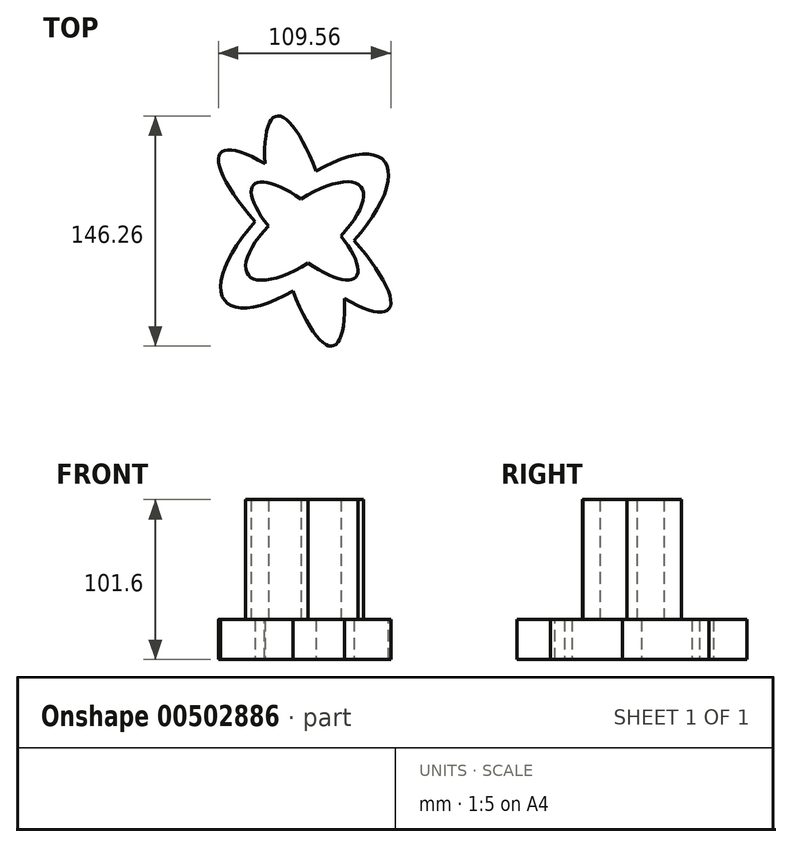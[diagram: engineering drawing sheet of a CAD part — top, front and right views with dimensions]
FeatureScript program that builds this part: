
annotation { "Feature Type Name" : "Feature", "Feature Type Description" : "" }
export const myFeature = defineFeature(function(context is Context, id is Id, definition is map)
    precondition{}
    {
        {
            var Q0;
            Q0=qCreatedBy(makeId("Top.planeOp"),FACE);
            var sketch = newSketch(context, id + "F0", { "sketchPlane" : qUnion([Q0])});
            skEllipse(sketch, "E0", {"center": v(0, 0) * mm, "majorRadius": 67.32 * mm, "minorRadius": 26.5 * mm, "majorAxis": v(0.75, 0.66)});
            skEllipse(sketch, "E1", {"center": v(0, 0) * mm, "majorRadius": 72.96 * mm, "minorRadius": 18.45 * mm, "majorAxis": v(-0.73, 0.68)});
            skSolve(sketch);
        }
        {
            var Q0;
            {var subQ0=sQuery(id+"F0.wireOp",EDGE,"E1");var subQ1=sQuery(id+"F0.wireOp",EDGE,"E0");var subQ2=makeQuery(id+"F0.imprint","INTERSECT",VERTEX,{"disambiguationData":[OD(1.0)],"derivedFrom":[subQ1,subQ0]});Q0=makeQuery(id+"F0.imprint","IMPRINT",FACE,{"disambiguationData":[TD([[makeQuery(id+"F0.imprint","IMPRINT",EDGE,{"disambiguationData":[TD([[subQ2,1.0]])],"derivedFrom":subQ1}),1.0]])]});}
            var Q1;
            {var subQ0=sQuery(id+"F0.wireOp",EDGE,"E1");var subQ1=sQuery(id+"F0.wireOp",EDGE,"E0");var subQ2=makeQuery(id+"F0.imprint","INTERSECT",VERTEX,{"disambiguationData":[OD(0.0)],"derivedFrom":[subQ1,subQ0]});Q1=makeQuery(id+"F0.imprint","IMPRINT",FACE,{"disambiguationData":[TD([[makeQuery(id+"F0.imprint","IMPRINT",EDGE,{"disambiguationData":[TD([[subQ2,1.0]])],"derivedFrom":subQ1}),1.0]])]});}
            var Q2;
            {var subQ0=sQuery(id+"F0.wireOp",EDGE,"E1");var subQ1=sQuery(id+"F0.wireOp",EDGE,"E0");var subQ2=makeQuery(id+"F0.imprint","INTERSECT",VERTEX,{"disambiguationData":[OD(0.0)],"derivedFrom":[subQ1,subQ0]});Q2=makeQuery(id+"F0.imprint","IMPRINT",FACE,{"disambiguationData":[TD([[makeQuery(id+"F0.imprint","IMPRINT",EDGE,{"disambiguationData":[TD([[subQ2,-1.0]])],"derivedFrom":subQ1}),1.0]])]});}
            var Q3;
            {var subQ0=sQuery(id+"F0.wireOp",EDGE,"E1");var subQ1=sQuery(id+"F0.wireOp",EDGE,"E0");var subQ2=makeQuery(id+"F0.imprint","INTERSECT",VERTEX,{"disambiguationData":[OD(0.0)],"derivedFrom":[subQ1,subQ0]});Q3=makeQuery(id+"F0.imprint","IMPRINT",FACE,{"disambiguationData":[TD([[makeQuery(id+"F0.imprint","IMPRINT",EDGE,{"disambiguationData":[TD([[subQ2,1.0]])],"derivedFrom":subQ1}),-1.0]])]});}
            var Q4;
            {var subQ0=sQuery(id+"F0.wireOp",EDGE,"E1");var subQ1=sQuery(id+"F0.wireOp",EDGE,"E0");var subQ2=makeQuery(id+"F0.imprint","INTERSECT",VERTEX,{"disambiguationData":[OD(2.0)],"derivedFrom":[subQ1,subQ0]});Q4=makeQuery(id+"F0.imprint","IMPRINT",FACE,{"disambiguationData":[TD([[makeQuery(id+"F0.imprint","IMPRINT",EDGE,{"disambiguationData":[TD([[subQ2,-1.0]])],"derivedFrom":subQ1}),-1.0]])]});}
            extrude(context, id + "F1", {"entities" : qUnion([Q0, Q1, Q2, Q3, Q4]), "depth" : 25.4 * mm});
        }
        {
            var Q0;
            Q0=qCreatedBy(makeId("Top.planeOp"),FACE);
            var sketch = newSketch(context, id + "F2", { "sketchPlane" : qUnion([Q0])});
            skEllipse(sketch, "E2", {"center": v(0, 0) * mm, "majorRadius": 45.4 * mm, "minorRadius": 17.82 * mm, "majorAxis": v(-0.79, -0.62)});
            skEllipse(sketch, "E3", {"center": v(0, 0) * mm, "majorRadius": 43.76 * mm, "minorRadius": 14.47 * mm, "majorAxis": v(0.74, -0.67)});
            skSolve(sketch);
        }
        {
            var Q0;
            {var subQ0=sQuery(id+"F2.wireOp",EDGE,"E3");var subQ1=sQuery(id+"F2.wireOp",EDGE,"E2");var subQ2=makeQuery(id+"F2.imprint","INTERSECT",VERTEX,{"disambiguationData":[OD(1.0)],"derivedFrom":[subQ1,subQ0]});Q0=makeQuery(id+"F2.imprint","IMPRINT",FACE,{"disambiguationData":[TD([[makeQuery(id+"F2.imprint","IMPRINT",EDGE,{"disambiguationData":[TD([[subQ2,1.0]])],"derivedFrom":subQ1}),1.0]])]});}
            var Q1;
            {var subQ0=sQuery(id+"F2.wireOp",EDGE,"E3");var subQ1=sQuery(id+"F2.wireOp",EDGE,"E2");var subQ2=makeQuery(id+"F2.imprint","INTERSECT",VERTEX,{"disambiguationData":[OD(0.0)],"derivedFrom":[subQ1,subQ0]});Q1=makeQuery(id+"F2.imprint","IMPRINT",FACE,{"disambiguationData":[TD([[makeQuery(id+"F2.imprint","IMPRINT",EDGE,{"disambiguationData":[TD([[subQ2,1.0]])],"derivedFrom":subQ1}),1.0]])]});}
            var Q2;
            {var subQ0=sQuery(id+"F2.wireOp",EDGE,"E3");var subQ1=sQuery(id+"F2.wireOp",EDGE,"E2");var subQ2=makeQuery(id+"F2.imprint","INTERSECT",VERTEX,{"disambiguationData":[OD(2.0)],"derivedFrom":[subQ1,subQ0]});Q2=makeQuery(id+"F2.imprint","IMPRINT",FACE,{"disambiguationData":[TD([[makeQuery(id+"F2.imprint","IMPRINT",EDGE,{"disambiguationData":[TD([[subQ2,-1.0]])],"derivedFrom":subQ1}),-1.0]])]});}
            var Q3;
            {var subQ0=sQuery(id+"F2.wireOp",EDGE,"E3");var subQ1=sQuery(id+"F2.wireOp",EDGE,"E2");var subQ2=makeQuery(id+"F2.imprint","INTERSECT",VERTEX,{"disambiguationData":[OD(0.0)],"derivedFrom":[subQ1,subQ0]});Q3=makeQuery(id+"F2.imprint","IMPRINT",FACE,{"disambiguationData":[TD([[makeQuery(id+"F2.imprint","IMPRINT",EDGE,{"disambiguationData":[TD([[subQ2,-1.0]])],"derivedFrom":subQ1}),1.0]])]});}
            var Q4;
            {var subQ0=sQuery(id+"F2.wireOp",EDGE,"E3");var subQ1=sQuery(id+"F2.wireOp",EDGE,"E2");var subQ2=makeQuery(id+"F2.imprint","INTERSECT",VERTEX,{"disambiguationData":[OD(0.0)],"derivedFrom":[subQ1,subQ0]});Q4=makeQuery(id+"F2.imprint","IMPRINT",FACE,{"disambiguationData":[TD([[makeQuery(id+"F2.imprint","IMPRINT",EDGE,{"disambiguationData":[TD([[subQ2,1.0]])],"derivedFrom":subQ1}),-1.0]])]});}
            extrude(context, id + "F3", {"entities" : qUnion([Q0, Q1, Q2, Q3, Q4]), "operationType" : NewBodyOperationType.ADD, "depth" : 25.4 * mm});
        }
        {
            var Q0;
            Q0 = qSketchRegion(id + "F2", true);
            extrude(context, id + "F4", {"entities" : qUnion([Q0]), "operationType" : NewBodyOperationType.ADD, "depth" : 76.2 * mm});
        }
        {
            var Q0;
            Q0=makeQuery(id+"F4.opExtrude","CAP_FACE",FACE,{"disambiguationData":[OSD([sQuery(id+"F2.wireOp",EDGE,"E2"),sQuery(id+"F2.wireOp",EDGE,"E3")])],"isStart":false});
            extrude(context, id + "F5", {"entities" : qUnion([Q0]), "operationType" : NewBodyOperationType.ADD, "depth" : 25.4 * mm});
        }
        {
            var Q0;
            Q0=qCreatedBy(makeId("Top.planeOp"),FACE);
            var sketch = newSketch(context, id + "F6", { "sketchPlane" : qUnion([Q0])});
            skEllipse(sketch, "E4", {"center": v(0, 0) * mm, "majorRadius": 75.17 * mm, "minorRadius": 18.44 * mm, "majorAxis": v(0.24, -0.97)});
            skSolve(sketch);
        }
        {
            var Q0;
            Q0=makeQuery(id+"F6.imprint","IMPRINT",FACE,{"disambiguationData":[TD([[makeQuery(id+"F6.imprint","IMPRINT",EDGE,{"derivedFrom":sQuery(id+"F6.wireOp",EDGE,"E4")}),1.0]])]});
            extrude(context, id + "F7", {"entities" : qUnion([Q0]), "operationType" : NewBodyOperationType.ADD, "depth" : 25.4 * mm});
        }
    });
